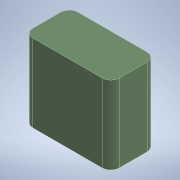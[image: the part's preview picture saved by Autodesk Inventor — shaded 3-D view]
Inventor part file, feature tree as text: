
AUTODESK INVENTOR PART (.ipt)
format: ipt  version: 2022 (Build 260153000, 153)  size: 250,368 bytes
history: native  units: mm
features: other x1, extrude x1, fillet x1, sketch x1
ambient origin geometry x8: Origin, YZ Plane, XZ Plane, XY Plane, X Axis, Y Axis, Z Axis, Center Point
bodies: Body1 (feature_tree)
feature tree (4):
  other  "Твердое тело1"
  extrude  "Выдавливание1"  Depth=10.0mm
  fillet  "Сопряжение1"  Radius=9.0mm
  sketch  "Эскиз1"
